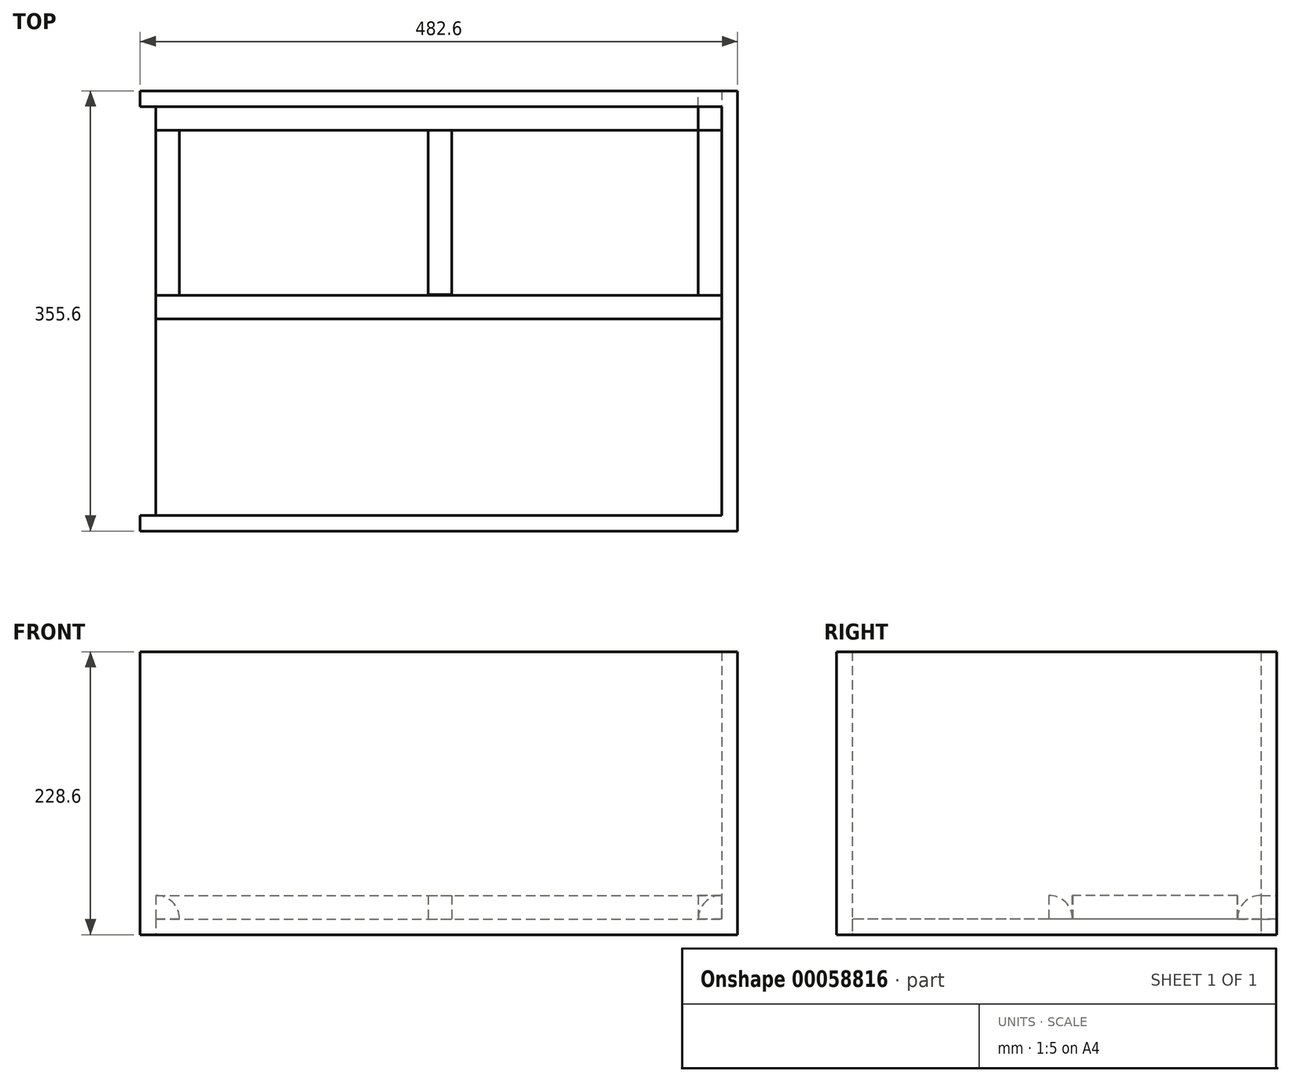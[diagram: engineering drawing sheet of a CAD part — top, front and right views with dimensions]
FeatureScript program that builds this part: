
annotation { "Feature Type Name" : "Feature", "Feature Type Description" : "" }
export const myFeature = defineFeature(function(context is Context, id is Id, definition is map)
    precondition{}
    {
        {
            var Q0;
            Q0=qCreatedBy(makeId("Top.planeOp"),FACE);
            var sketch = newSketch(context, id + "F0", { "sketchPlane" : qUnion([Q0])});
            skLineSegment(sketch, "E0.bottom", {"start": v(-407.63, 159.62) * mm, "end": v(49.57, 159.62) * mm});
            skLineSegment(sketch, "E0.top", {"start": v(-407.63, -170.58) * mm, "end": v(49.57, -170.58) * mm});
            skLineSegment(sketch, "E0.left", {"start": v(-407.63, 159.62) * mm, "end": v(-407.63, -170.58) * mm});
            skLineSegment(sketch, "E0.right", {"start": v(49.57, 159.62) * mm, "end": v(49.57, -170.58) * mm});
            skLineSegment(sketch, "E1.top", {"start": v(-420.57, 159.62) * mm, "end": v(49.57, 159.62) * mm});
            skLineSegment(sketch, "E1.right", {"start": v(49.57, 159.62) * mm, "end": v(49.57, 159.62) * mm});
            skLineSegment(sketch, "E2.bottom", {"start": v(49.57, 159.62) * mm, "end": v(62.27, 159.62) * mm});
            skLineSegment(sketch, "E2.top", {"start": v(49.57, -170.58) * mm, "end": v(62.27, -170.58) * mm});
            skLineSegment(sketch, "E2.right", {"start": v(62.27, 159.62) * mm, "end": v(62.27, -170.58) * mm});
            skLineSegment(sketch, "E3.bottom", {"start": v(-407.63, -170.58) * mm, "end": v(-420.33, -170.58) * mm});
            skLineSegment(sketch, "E3.top", {"start": v(-407.63, 159.62) * mm, "end": v(-420.33, 159.62) * mm});
            skLineSegment(sketch, "E3.left", {"start": v(-407.63, -170.58) * mm, "end": v(-407.63, 159.62) * mm});
            skLineSegment(sketch, "E3.right", {"start": v(-420.33, -170.58) * mm, "end": v(-420.33, 159.62) * mm});
            skLineSegment(sketch, "E4.bottom", {"start": v(-420.33, 159.62) * mm, "end": v(62.27, 159.62) * mm});
            skLineSegment(sketch, "E4.top", {"start": v(-420.33, 172.32) * mm, "end": v(62.27, 172.32) * mm});
            skLineSegment(sketch, "E4.left", {"start": v(-420.33, 159.62) * mm, "end": v(-420.33, 172.32) * mm});
            skLineSegment(sketch, "E4.right", {"start": v(62.27, 159.62) * mm, "end": v(62.27, 172.32) * mm});
            skLineSegment(sketch, "E5.bottom", {"start": v(-420.33, -170.58) * mm, "end": v(62.27, -170.58) * mm});
            skLineSegment(sketch, "E5.top", {"start": v(-420.33, -183.28) * mm, "end": v(62.27, -183.28) * mm});
            skLineSegment(sketch, "E5.left", {"start": v(-420.33, -170.58) * mm, "end": v(-420.33, -183.28) * mm});
            skLineSegment(sketch, "E5.right", {"start": v(62.27, -170.58) * mm, "end": v(62.27, -183.28) * mm});
            skSolve(sketch);
        }
        {
            var Q0;
            {var subQ0=sQuery(id+"F0.wireOp",EDGE,"E0.right");Q0=makeQuery(id+"F0.imprint","IMPRINT",FACE,{"disambiguationData":[TD([[makeQuery(id+"F0.imprint","IMPRINT",EDGE,{"derivedFrom":subQ0}),-1.0]])]});}
            extrude(context, id + "F1", {"entities" : qUnion([Q0]), "depth" : 12.7 * mm});
        }
        {
            var Q0;
            Q0=makeQuery(id+"F0.imprint","IMPRINT",FACE,{"disambiguationData":[TD([[makeQuery(id+"F0.imprint","IMPRINT",EDGE,{"derivedFrom":sQuery(id+"F0.wireOp",EDGE,"E4.top")}),-1.0]])]});
            var Q1;
            {var subQ0=sQuery(id+"F0.wireOp",EDGE,"E3.left");Q1=makeQuery(id+"F0.imprint","IMPRINT",FACE,{"disambiguationData":[TD([[makeQuery(id+"F0.imprint","IMPRINT",EDGE,{"derivedFrom":subQ0}),1.0]])]});}
            var Q2;
            Q2=makeQuery(id+"F0.imprint","IMPRINT",FACE,{"disambiguationData":[TD([[makeQuery(id+"F0.imprint","IMPRINT",EDGE,{"derivedFrom":sQuery(id+"F0.wireOp",EDGE,"E5.top")}),1.0]])]});
            var Q3;
            {var subQ0=sQuery(id+"F0.wireOp",EDGE,"E0.right");Q3=makeQuery(id+"F0.imprint","IMPRINT",FACE,{"disambiguationData":[TD([[makeQuery(id+"F0.imprint","IMPRINT",EDGE,{"derivedFrom":subQ0}),1.0]])]});}
            extrude(context, id + "F2", {"entities" : qUnion([Q0, Q1, Q2, Q3]), "operationType" : NewBodyOperationType.ADD, "depth" : 228.6 * mm});
        }
        {
            var Q0;
            Q0=makeQuery(id+"F1.opExtrude","CAP_FACE",FACE,{"disambiguationData":[OSD([sQuery(id+"F0.wireOp",EDGE,"E0.right"),sQuery(id+"F0.wireOp",EDGE,"E3.left"),sQuery(id+"F0.wireOp",EDGE,"E4.bottom"),sQuery(id+"F0.wireOp",EDGE,"E5.bottom")])],"isStart":false});
            var sketch = newSketch(context, id + "F3", { "sketchPlane" : qUnion([Q0])});
            skLineSegment(sketch, "E6.bottom", {"start": v(-407.63, 159.62) * mm, "end": v(49.57, 159.62) * mm});
            skLineSegment(sketch, "E6.top", {"start": v(-407.63, 140.57) * mm, "end": v(49.57, 140.57) * mm});
            skLineSegment(sketch, "E6.left", {"start": v(-407.63, 159.62) * mm, "end": v(-407.63, 140.57) * mm});
            skLineSegment(sketch, "E6.right", {"start": v(49.57, 159.62) * mm, "end": v(49.57, 140.57) * mm});
            skLineSegment(sketch, "E7", {"start": v(30.52, 159.62) * mm, "end": v(30.52, 0) * mm, "construction": true});
            skLineSegment(sketch, "E8", {"start": v(-166.33, 191.41) * mm, "end": v(-166.33, 0) * mm, "construction": true});
            skLineSegment(sketch, "E9", {"start": v(-191.73, 191.41) * mm, "end": v(-191.73, 0) * mm, "construction": true});
            skLineSegment(sketch, "E10", {"start": v(-388.58, 191.41) * mm, "end": v(-388.58, 0) * mm, "construction": true});
            skLineSegment(sketch, "E11", {"start": v(30.52, 7.22) * mm, "end": v(-388.58, 7.22) * mm, "construction": true});
            skLineSegment(sketch, "E12", {"start": v(-178.65, 191.41) * mm, "end": v(-178.65, 0) * mm, "construction": true});
            skSolve(sketch);
        }
        {
            var Q0;
            Q0=makeQuery(id+"F3.imprint","IMPRINT",FACE,{"disambiguationData":[TD([[makeQuery(id+"F3.imprint","IMPRINT",EDGE,{"derivedFrom":sQuery(id+"F3.wireOp",EDGE,"E6.bottom")}),-1.0]])]});
            extrude(context, id + "F4", {"entities" : qUnion([Q0]), "depth" : 19.05 * mm});
        }
        {
            var Q0;
            Q0=makeQuery(id+"F4.opExtrude","SWEPT_BODY",BODY,{"disambiguationData":[OSD([sQuery(id+"F3.wireOp",EDGE,"E6.bottom"),sQuery(id+"F3.wireOp",EDGE,"E6.top"),sQuery(id+"F3.wireOp",EDGE,"E6.left"),sQuery(id+"F3.wireOp",EDGE,"E6.right")])]});
            transform(context, id + "F5", {"entities" : qUnion([Q0]), "transformType" : TransformType.TRANSLATION_3D, "dx" : 0 * mm, "dy" : -152.4 * mm, "dz" : 0 * mm, "makeCopy" : true});
        }
        {
            var Q0;
            Q0=makeQuery(id+"F5.opPattern","COPY",BODY,{"derivedFrom":makeQuery(id+"F4.opExtrude","SWEPT_BODY",BODY,{"disambiguationData":[OSD([sQuery(id+"F3.wireOp",EDGE,"E6.bottom"),sQuery(id+"F3.wireOp",EDGE,"E6.top"),sQuery(id+"F3.wireOp",EDGE,"E6.left"),sQuery(id+"F3.wireOp",EDGE,"E6.right")])]}),"instanceName":"1"});
            var Q1;
            Q1=makeQuery(id+"F5.opPattern","COPY",EDGE,{"derivedFrom":makeQuery(id+"F4.opExtrude","SWEPT_EDGE",EDGE,{"disambiguationData":[OSD([sQuery(id+"F3.wireOp",EDGE,"E6.bottom"),sQuery(id+"F3.wireOp",EDGE,"E6.right")])]}),"instanceName":"1"});
            transform(context, id + "F6", {"entities" : qUnion([Q0]), "transformType" : TransformType.ROTATION, "transformAxis" : qUnion([Q1]), "angle" : 90 * degree, "makeCopy" : true});
        }
        {
            var Q0;
            Q0=makeQuery(id+"F6.opPattern","COPY",FACE,{"derivedFrom":makeQuery(id+"F5.opPattern","COPY",FACE,{"derivedFrom":makeQuery(id+"F4.opExtrude","SWEPT_FACE",FACE,{"disambiguationData":[OSD([sQuery(id+"F3.wireOp",EDGE,"E6.left")])]}),"instanceName":"1"}),"instanceName":"1"});
            var Q1;
            Q1=makeQuery(id+"F4.opExtrude","SWEPT_FACE",FACE,{"disambiguationData":[OSD([sQuery(id+"F3.wireOp",EDGE,"E6.top")])]});
            extrude(context, id + "F7", {"entities" : qUnion([Q0]), "operationType" : NewBodyOperationType.REMOVE, "endBound" : BoundingType.UP_TO_SURFACE, "oppositeDirection" : true, "endBoundEntityFace" : qUnion([Q1]), "depth" : 99.4 * mm});
        }
        {
            var Q0;
            Q0=makeQuery(id+"F6.opPattern","COPY",BODY,{"derivedFrom":makeQuery(id+"F5.opPattern","COPY",BODY,{"derivedFrom":makeQuery(id+"F4.opExtrude","SWEPT_BODY",BODY,{"disambiguationData":[OSD([sQuery(id+"F3.wireOp",EDGE,"E6.bottom"),sQuery(id+"F3.wireOp",EDGE,"E6.top"),sQuery(id+"F3.wireOp",EDGE,"E6.left"),sQuery(id+"F3.wireOp",EDGE,"E6.right")])]}),"instanceName":"1"}),"instanceName":"1"});
            transform(context, id + "F8", {"entities" : qUnion([Q0]), "transformType" : TransformType.TRANSLATION_3D, "dx" : -400.05 * mm, "dy" : 0 * mm, "dz" : 0 * mm, "makeCopy" : true});
        }
        {
            var Q0;
            Q0=makeQuery(id+"F4.opExtrude","CAP_EDGE",EDGE,{"disambiguationData":[OSD([sQuery(id+"F3.wireOp",EDGE,"E6.top")])],"isStart":false});
            var Q1;
            Q1=makeQuery(id+"F8.opPattern","COPY",EDGE,{"derivedFrom":makeQuery(id+"F6.opPattern","COPY",EDGE,{"derivedFrom":makeQuery(id+"F5.opPattern","COPY",EDGE,{"derivedFrom":makeQuery(id+"F4.opExtrude","CAP_EDGE",EDGE,{"disambiguationData":[OSD([sQuery(id+"F3.wireOp",EDGE,"E6.bottom")])],"isStart":false}),"instanceName":"1"}),"instanceName":"1"}),"instanceName":"1"});
            var Q2;
            Q2=makeQuery(id+"F6.opPattern","COPY",EDGE,{"derivedFrom":makeQuery(id+"F5.opPattern","COPY",EDGE,{"derivedFrom":makeQuery(id+"F4.opExtrude","CAP_EDGE",EDGE,{"disambiguationData":[OSD([sQuery(id+"F3.wireOp",EDGE,"E6.top")])],"isStart":false}),"instanceName":"1"}),"instanceName":"1"});
            var Q3;
            Q3=makeQuery(id+"F5.opPattern","COPY",EDGE,{"derivedFrom":makeQuery(id+"F4.opExtrude","CAP_EDGE",EDGE,{"disambiguationData":[OSD([sQuery(id+"F3.wireOp",EDGE,"E6.bottom")])],"isStart":false}),"instanceName":"1"});
            fillet(context, id + "F9", {"entities" : qUnion([Q0, Q1, Q2, Q3]), "radius" : 19.05 * mm, "tangentPropagation" : true, "allowEdgeOverflow" : false});
        }
        {
            var Q0;
            Q0=makeQuery(id+"F8.opPattern","COPY",BODY,{"derivedFrom":makeQuery(id+"F6.opPattern","COPY",BODY,{"derivedFrom":makeQuery(id+"F5.opPattern","COPY",BODY,{"derivedFrom":makeQuery(id+"F4.opExtrude","SWEPT_BODY",BODY,{"disambiguationData":[OSD([sQuery(id+"F3.wireOp",EDGE,"E6.bottom"),sQuery(id+"F3.wireOp",EDGE,"E6.top"),sQuery(id+"F3.wireOp",EDGE,"E6.left"),sQuery(id+"F3.wireOp",EDGE,"E6.right")])]}),"instanceName":"1"}),"instanceName":"1"}),"instanceName":"1"});
            var Q1;
            Q1=makeQuery(id+"F9.opFillet","BLEND_VERTEX",VERTEX,{"blendedFrom":[makeQuery(id+"F8.opPattern","COPY",EDGE,{"derivedFrom":makeQuery(id+"F6.opPattern","COPY",EDGE,{"derivedFrom":makeQuery(id+"F5.opPattern","COPY",EDGE,{"derivedFrom":makeQuery(id+"F4.opExtrude","CAP_EDGE",EDGE,{"disambiguationData":[OSD([sQuery(id+"F3.wireOp",EDGE,"E6.bottom")])],"isStart":false}),"instanceName":"1"}),"instanceName":"1"}),"instanceName":"1"}),makeQuery(id+"F8.opPattern","COPY",FACE,{"derivedFrom":makeQuery(id+"F7.boolean.opBoolean","COPY",FACE,{"derivedFrom":makeQuery(id+"F7.opExtrude","CAP_FACE",FACE,{"disambiguationData":[OSD([sQuery(id+"F3.wireOp",EDGE,"E6.left")])],"isStart":false})}),"instanceName":"1"}),makeQuery(id+"F8.opPattern","COPY",FACE,{"derivedFrom":makeQuery(id+"F6.opPattern","COPY",FACE,{"derivedFrom":makeQuery(id+"F5.opPattern","COPY",FACE,{"derivedFrom":makeQuery(id+"F4.opExtrude","SWEPT_FACE",FACE,{"disambiguationData":[OSD([sQuery(id+"F3.wireOp",EDGE,"E6.top")])]}),"instanceName":"1"}),"instanceName":"1"}),"instanceName":"1"})],"blendedInto":[makeQuery(id+"F8.opPattern","COPY",FACE,{"derivedFrom":makeQuery(id+"F7.boolean.opBoolean","COPY",FACE,{"derivedFrom":makeQuery(id+"F7.opExtrude","CAP_FACE",FACE,{"disambiguationData":[OSD([sQuery(id+"F3.wireOp",EDGE,"E6.left")])],"isStart":false})}),"instanceName":"1"}),makeQuery(id+"F8.opPattern","COPY",FACE,{"derivedFrom":makeQuery(id+"F6.opPattern","COPY",FACE,{"derivedFrom":makeQuery(id+"F5.opPattern","COPY",FACE,{"derivedFrom":makeQuery(id+"F4.opExtrude","SWEPT_FACE",FACE,{"disambiguationData":[OSD([sQuery(id+"F3.wireOp",EDGE,"E6.top")])]}),"instanceName":"1"}),"instanceName":"1"}),"instanceName":"1"})]});
            var Q2;
            Q2=sQuery(id+"F3.wireOp",VERTEX,"E6.left.end");
            transform(context, id + "F10", {"entities" : qUnion([Q0]), "transformType" : TransformType.TRANSLATION_ENTITY, "oppositeDirectionEntity" : false, "transformLine" : qUnion([Q1, Q2]), "makeCopy" : false});
        }
        {
            var Q0;
            Q0=makeQuery(id+"F8.opPattern","COPY",BODY,{"derivedFrom":makeQuery(id+"F6.opPattern","COPY",BODY,{"derivedFrom":makeQuery(id+"F5.opPattern","COPY",BODY,{"derivedFrom":makeQuery(id+"F4.opExtrude","SWEPT_BODY",BODY,{"disambiguationData":[OSD([sQuery(id+"F3.wireOp",EDGE,"E6.bottom"),sQuery(id+"F3.wireOp",EDGE,"E6.top"),sQuery(id+"F3.wireOp",EDGE,"E6.left"),sQuery(id+"F3.wireOp",EDGE,"E6.right")])]}),"instanceName":"1"}),"instanceName":"1"}),"instanceName":"1"});
            var Q1;
            Q1=makeQuery(id+"F8.opPattern","COPY",VERTEX,{"derivedFrom":makeQuery(id+"F6.opPattern","COPY",VERTEX,{"derivedFrom":makeQuery(id+"F5.opPattern","COPY",VERTEX,{"derivedFrom":makeQuery(id+"F4.opExtrude","CAP_VERTEX",VERTEX,{"disambiguationData":[OSD([sQuery(id+"F0.wireOp",EDGE,"3e18e163-0115-4f58-8c5f-c37865d85116.left"),sQuery(id+"F3.wireOp",EDGE,"E6.top"),sQuery(id+"F3.wireOp",EDGE,"E6.right")])],"isStart":true}),"instanceName":"1"}),"instanceName":"1"}),"instanceName":"1"});
            var Q2;
            Q2=makeQuery(id+"F5.opPattern","COPY",VERTEX,{"derivedFrom":makeQuery(id+"F4.opExtrude","CAP_VERTEX",VERTEX,{"disambiguationData":[OSD([sQuery(id+"F3.wireOp",EDGE,"E6.top"),sQuery(id+"F3.wireOp",EDGE,"E6.left")])],"isStart":true}),"instanceName":"1"});
            transform(context, id + "F11", {"entities" : qUnion([Q0]), "transformType" : TransformType.TRANSLATION_ENTITY, "oppositeDirectionEntity" : false, "transformLine" : qUnion([Q1, Q2]), "makeCopy" : false});
        }
        {
            var Q0;
            Q0=makeQuery(id+"F8.opPattern","COPY",BODY,{"derivedFrom":makeQuery(id+"F6.opPattern","COPY",BODY,{"derivedFrom":makeQuery(id+"F5.opPattern","COPY",BODY,{"derivedFrom":makeQuery(id+"F4.opExtrude","SWEPT_BODY",BODY,{"disambiguationData":[OSD([sQuery(id+"F3.wireOp",EDGE,"E6.bottom"),sQuery(id+"F3.wireOp",EDGE,"E6.top"),sQuery(id+"F3.wireOp",EDGE,"E6.left"),sQuery(id+"F3.wireOp",EDGE,"E6.right")])]}),"instanceName":"1"}),"instanceName":"1"}),"instanceName":"1"});
            var Q1;
            {var subQ0=sQuery(id+"F3.wireOp",EDGE,"E6.left");var subQ1=sQuery(id+"F3.wireOp",EDGE,"E6.top");var subQ2=sQuery(id+"F0.wireOp",EDGE,"E3.left");Q1=makeQuery(id+"F8.opPattern","COPY",VERTEX,{"derivedFrom":makeQuery(id+"F7.boolean.opBoolean","COPY",VERTEX,{"derivedFrom":makeQuery(id+"F7.opExtrude","CAP_VERTEX",VERTEX,{"disambiguationData":[OSD([subQ2,subQ1,subQ0]),TDD([makeQuery(id+"F6.opPattern","COPY",EDGE,{"derivedFrom":makeQuery(id+"F5.opPattern","COPY",EDGE,{"derivedFrom":makeQuery(id+"F4.opExtrude","SWEPT_EDGE",EDGE,{"disambiguationData":[OSD([subQ2,subQ1,subQ0])]}),"instanceName":"1"}),"instanceName":"1"}),makeQuery(id+"F6.opPattern","COPY",EDGE,{"derivedFrom":makeQuery(id+"F5.opPattern","COPY",EDGE,{"derivedFrom":makeQuery(id+"F4.opExtrude","CAP_EDGE",EDGE,{"disambiguationData":[OSD([subQ0])],"isStart":true}),"instanceName":"1"}),"instanceName":"1"})])],"isStart":false})}),"instanceName":"1"});}
            var Q2;
            Q2=sQuery(id+"F3.wireOp",VERTEX,"E6.left.end");
            transform(context, id + "F12", {"entities" : qUnion([Q0]), "transformType" : TransformType.TRANSLATION_ENTITY, "oppositeDirectionEntity" : false, "transformLine" : qUnion([Q1, Q2]), "makeCopy" : false});
        }
        {
            var Q0;
            {var subQ0=sQuery(id+"F3.wireOp",EDGE,"E6.top");Q0=makeQuery(id+"F3.imprint","IMPRINT",FACE,{"disambiguationData":[TD([[makeQuery(id+"F3.imprint","IMPRINT",EDGE,{"derivedFrom":subQ0}),-1.0]])]});}
            var sketch = newSketch(context, id + "F13", { "sketchPlane" : qUnion([Q0])});
            skLineSegment(sketch, "E13.bottom", {"start": v(-187.65, 140.35) * mm, "end": v(-168.6, 140.35) * mm});
            skLineSegment(sketch, "E13.top", {"start": v(-187.65, 7.6) * mm, "end": v(-168.6, 7.6) * mm});
            skLineSegment(sketch, "E13.left", {"start": v(-187.65, 140.35) * mm, "end": v(-187.65, 7.6) * mm});
            skLineSegment(sketch, "E13.right", {"start": v(-168.6, 140.35) * mm, "end": v(-168.6, 7.6) * mm});
            skSolve(sketch);
        }
        {
            var Q0;
            Q0 = qSketchRegion(id + "F13", true);
            extrude(context, id + "F14", {"entities" : qUnion([Q0]), "depth" : 19.05 * mm});
        }
    });
